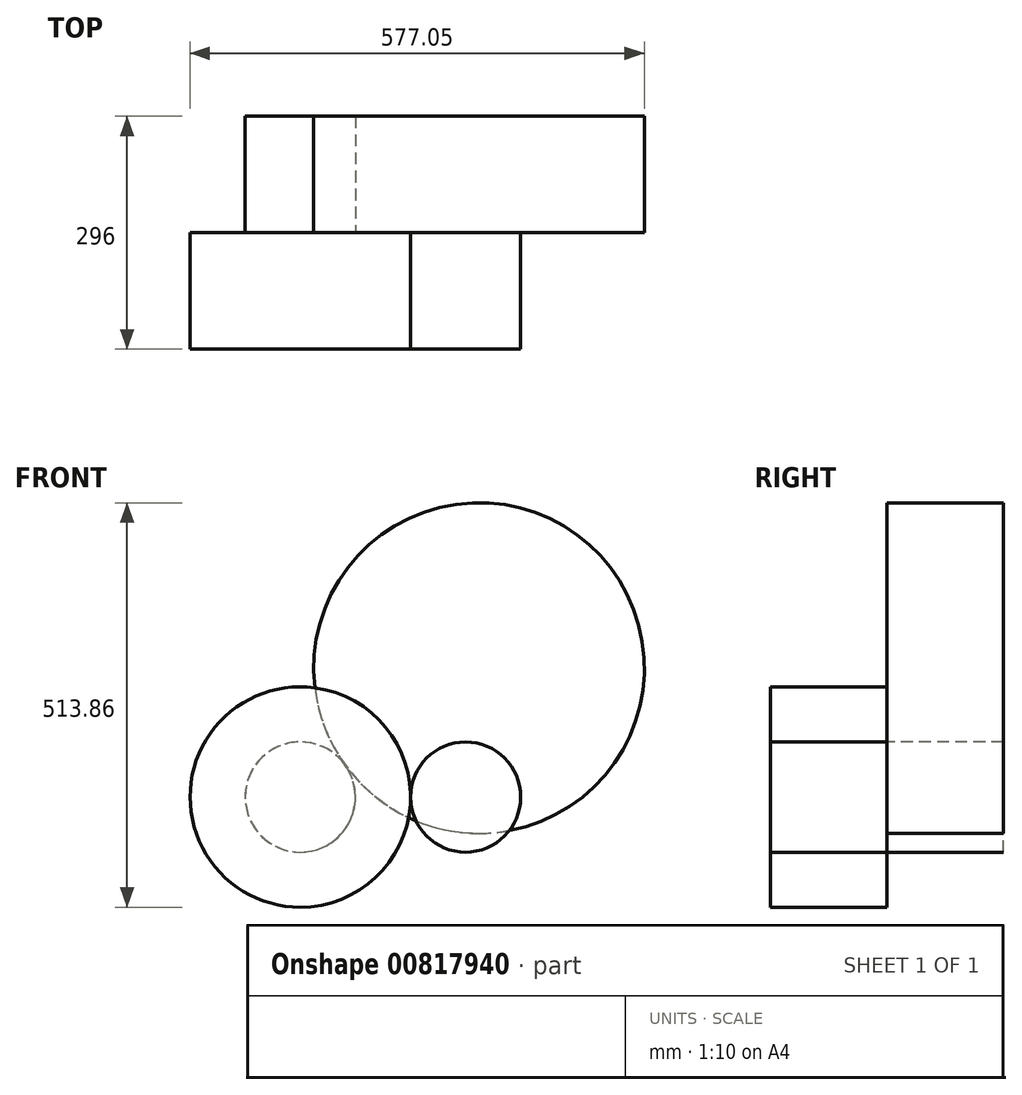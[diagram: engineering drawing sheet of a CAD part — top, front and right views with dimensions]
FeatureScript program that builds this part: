
annotation { "Feature Type Name" : "Feature", "Feature Type Description" : "" }
export const myFeature = defineFeature(function(context is Context, id is Id, definition is map)
    precondition{}
    {
        {
            var Q0;
            Q0=qCreatedBy(makeId("Front.planeOp"),FACE);
            var sketch = newSketch(context, id + "F0", { "sketchPlane" : qUnion([Q0])});
            skCircle(sketch, "E0", {"center": v(0, 0) * mm, "radius": 70 * mm});
            skSolve(sketch);
        }
        {
            var Q0;
            Q0 = qSketchRegion(id + "F0", true);
            extrude(context, id + "F1", {"entities" : qUnion([Q0]), "depth" : 148 * mm, "offsetDistance" : 25 * mm});
        }
        {
            var Q0;
            Q0=qCreatedBy(makeId("Front.planeOp"),FACE);
            var sketch = newSketch(context, id + "F2", { "sketchPlane" : qUnion([Q0])});
            skCircle(sketch, "E1", {"center": v(-210, 0) * mm, "radius": 140 * mm});
            skSolve(sketch);
        }
        {
            var Q0;
            Q0=makeQuery(id+"F2.imprint","IMPRINT",FACE,{"disambiguationData":[TD([[makeQuery(id+"F2.imprint","IMPRINT",EDGE,{"derivedFrom":sQuery(id+"F2.wireOp",EDGE,"E1")}),1.0]])]});
            extrude(context, id + "F3", {"entities" : qUnion([Q0]), "operationType" : NewBodyOperationType.ADD, "depth" : 148 * mm, "offsetDistance" : 25 * mm});
        }
        {
            var Q0;
            Q0=qCreatedBy(makeId("Front.planeOp"),FACE);
            var sketch = newSketch(context, id + "F4", { "sketchPlane" : qUnion([Q0])});
            skCircle(sketch, "E2", {"center": v(-210, 0) * mm, "radius": 70 * mm});
            skCircle(sketch, "E3", {"center": v(17.05, 163.86) * mm, "radius": 210 * mm});
            skSolve(sketch);
        }
        {
            var Q0;
            Q0 = qSketchRegion(id + "F4", true);
            extrude(context, id + "F5", {"entities" : qUnion([Q0]), "operationType" : NewBodyOperationType.ADD, "oppositeDirection" : true, "depth" : 148 * mm, "offsetDistance" : 25 * mm});
        }
        {
            var Q0;
            Q0 = qSketchRegion(id + "F4", true);
            extrude(context, id + "F6", {"entities" : qUnion([Q0]), "oppositeDirection" : true, "depth" : 148 * mm, "offsetDistance" : 25 * mm});
        }
    });
